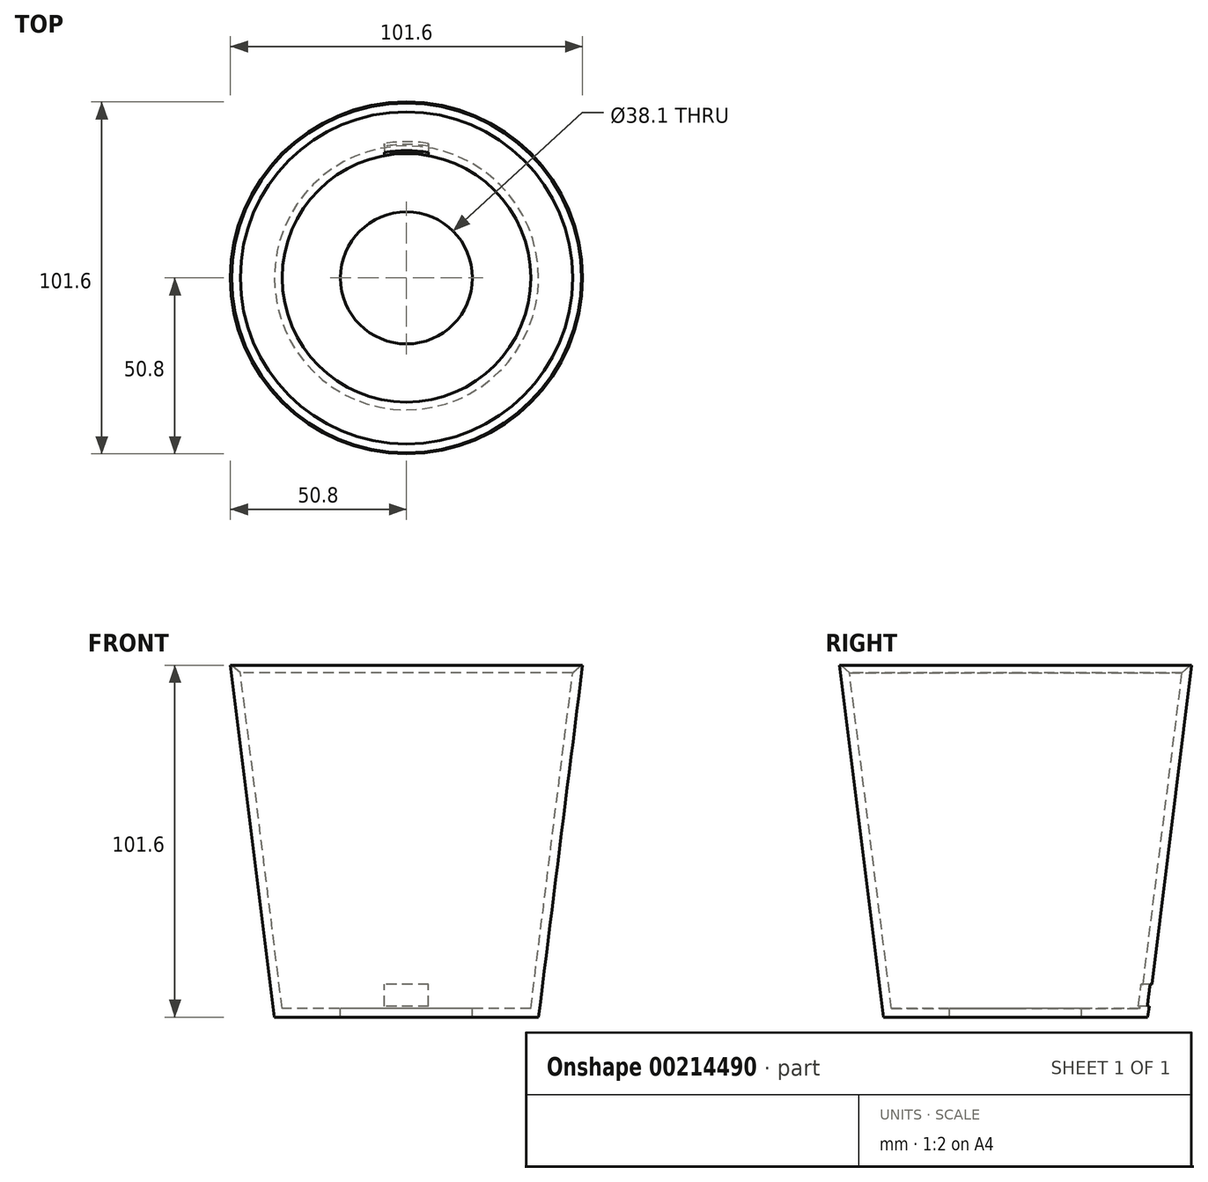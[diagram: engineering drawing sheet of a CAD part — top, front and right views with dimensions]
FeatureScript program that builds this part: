
annotation { "Feature Type Name" : "Feature", "Feature Type Description" : "" }
export const myFeature = defineFeature(function(context is Context, id is Id, definition is map)
    precondition{}
    {
        {
            var Q0;
            Q0=qCreatedBy(makeId("Top.planeOp"),FACE);
            var sketch = newSketch(context, id + "F0", { "sketchPlane" : qUnion([Q0])});
            skCircle(sketch, "E0", {"center": v(0, 0) * mm, "radius": 38.1 * mm});
            skSolve(sketch);
        }
        {
            var Q0;
            Q0=qCreatedBy(makeId("Top.planeOp"),FACE);
            cPlane(context, id + "F1", {"entities" : qUnion([Q0]), "cplaneType" : CPlaneType.OFFSET, "offset" : 101.6 * mm, "width" : 152.4 * mm, "height" : 152.4 * mm});
        }
        {
            var Q0;
            Q0=qCreatedBy(id+"F1.planeOp",FACE);
            var sketch = newSketch(context, id + "F2", { "sketchPlane" : qUnion([Q0])});
            skCircle(sketch, "E1", {"center": v(0, 0) * mm, "radius": 50.8 * mm});
            skSolve(sketch);
        }
        {
            var Q0;
            Q0=makeQuery(id+"F2.imprint","IMPRINT",FACE,{"disambiguationData":[TD([[makeQuery(id+"F2.imprint","IMPRINT",EDGE,{"derivedFrom":sQuery(id+"F2.wireOp",EDGE,"E1")}),1.0]])]});
            var Q1;
            Q1=makeQuery(id+"F0.imprint","IMPRINT",FACE,{"disambiguationData":[TD([[makeQuery(id+"F0.imprint","IMPRINT",EDGE,{"derivedFrom":sQuery(id+"F0.wireOp",EDGE,"E0")}),1.0]])]});
            loft(context, id + "F3", {"sheetProfilesArray" : [{ "sheetProfileEntities" : qUnion([Q0]) }, { "sheetProfileEntities" : qUnion([Q1]) }]});
        }
        {
            var Q0;
            Q0=makeQuery(id+"F3.opLoft","CAP_FACE",FACE,{"disambiguationData":[OSD([makeQuery(id+"F2.imprint","IMPRINT",FACE,{"disambiguationData":[TD([[makeQuery(id+"F2.imprint","IMPRINT",EDGE,{"derivedFrom":sQuery(id+"F2.wireOp",EDGE,"E1")}),1.0]])]})])],"isStart":true});
            shell(context, id + "F4", {"entities" : qUnion([Q0]), "thickness" : 2.54 * mm});
        }
        {
            var Q0;
            Q0=qCreatedBy(makeId("Front.planeOp"),FACE);
            var sketch = newSketch(context, id + "F5", { "sketchPlane" : qUnion([Q0])});
            skLineSegment(sketch, "E2.bottom", {"start": v(6.35, 9.53) * mm, "end": v(-6.35, 9.53) * mm});
            skLineSegment(sketch, "E2.top", {"start": v(6.35, 3.18) * mm, "end": v(-6.35, 3.17) * mm});
            skLineSegment(sketch, "E2.left", {"start": v(6.35, 9.53) * mm, "end": v(6.35, 3.17) * mm});
            skLineSegment(sketch, "E2.right", {"start": v(-6.35, 9.53) * mm, "end": v(-6.35, 3.17) * mm});
            skSolve(sketch);
        }
        {
            var Q0;
            Q0 = qSketchRegion(id + "F5", true);
            extrude(context, id + "F6", {"entities" : qUnion([Q0]), "operationType" : NewBodyOperationType.REMOVE, "oppositeDirection" : true, "depth" : 40.13 * mm});
        }
        {
            var Q0;
            Q0=makeQuery(id+"F4.opShell","OFFSET_EDGE",EDGE,{"disambiguationData":[OSD([sQuery(id+"F2.wireOp",EDGE,"E1")])]});
            chamfer(context, id + "F7", {"entities" : qUnion([Q0]), "width" : 2.54 * mm, "tangentPropagation" : true});
        }
        {
            var Q0;
            Q0=makeQuery(id+"F4.opShell","OFFSET_FACE",FACE,{"disambiguationData":[OSD([makeQuery(id+"F0.imprint","IMPRINT",FACE,{"disambiguationData":[TD([[makeQuery(id+"F0.imprint","IMPRINT",EDGE,{"derivedFrom":sQuery(id+"F0.wireOp",EDGE,"E0")}),1.0]])]})])]});
            var sketch = newSketch(context, id + "F8", { "sketchPlane" : qUnion([Q0])});
            skCircle(sketch, "E3", {"center": v(0, 0) * mm, "radius": 19.05 * mm});
            skSolve(sketch);
        }
        {
            var Q0;
            Q0=makeQuery(id+"F8.imprint","IMPRINT",FACE,{"disambiguationData":[TD([[makeQuery(id+"F8.imprint","IMPRINT",EDGE,{"derivedFrom":sQuery(id+"F8.wireOp",EDGE,"E3")}),1.0]])]});
            extrude(context, id + "F9", {"entities" : qUnion([Q0]), "operationType" : NewBodyOperationType.REMOVE, "oppositeDirection" : true, "depth" : 25.4 * mm});
        }
    });
